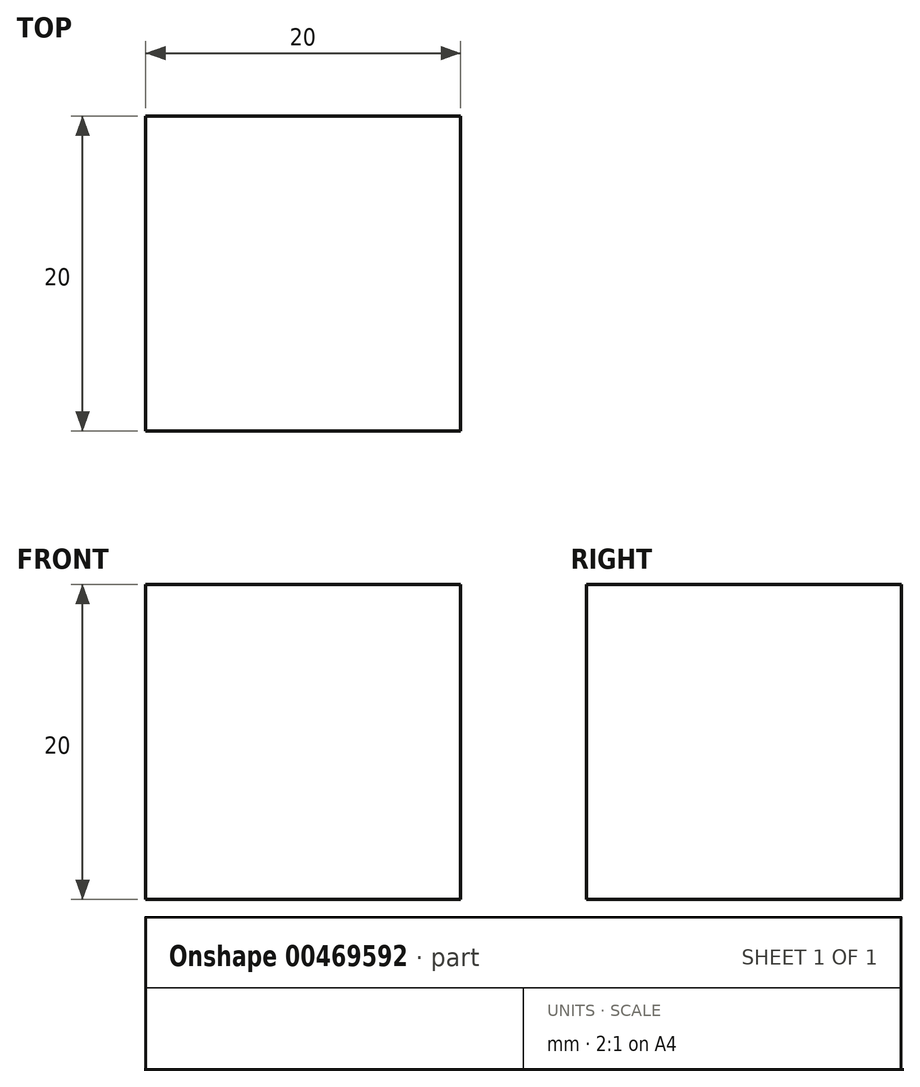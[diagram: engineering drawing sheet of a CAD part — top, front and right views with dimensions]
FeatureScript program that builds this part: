
annotation { "Feature Type Name" : "Feature", "Feature Type Description" : "" }
export const myFeature = defineFeature(function(context is Context, id is Id, definition is map)
    precondition{}
    {
        {
            var Q0;
            Q0=qCreatedBy(makeId("Right.planeOp"),FACE);
            var sketch = newSketch(context, id + "F0", { "sketchPlane" : qUnion([Q0])});
            skLineSegment(sketch, "E0.bottom", {"start": v(0, 0) * mm, "end": v(20, 0) * mm});
            skLineSegment(sketch, "E0.top", {"start": v(0, 20) * mm, "end": v(20, 20) * mm});
            skLineSegment(sketch, "E0.left", {"start": v(0, 0) * mm, "end": v(0, 20) * mm});
            skLineSegment(sketch, "E0.right", {"start": v(20, 0) * mm, "end": v(20, 20) * mm});
            skSolve(sketch);
        }
        {
            var Q0;
            Q0 = qSketchRegion(id + "F0", true);
            extrude(context, id + "F1", {"entities" : qUnion([Q0]), "depth" : 20 * mm});
        }
    });
